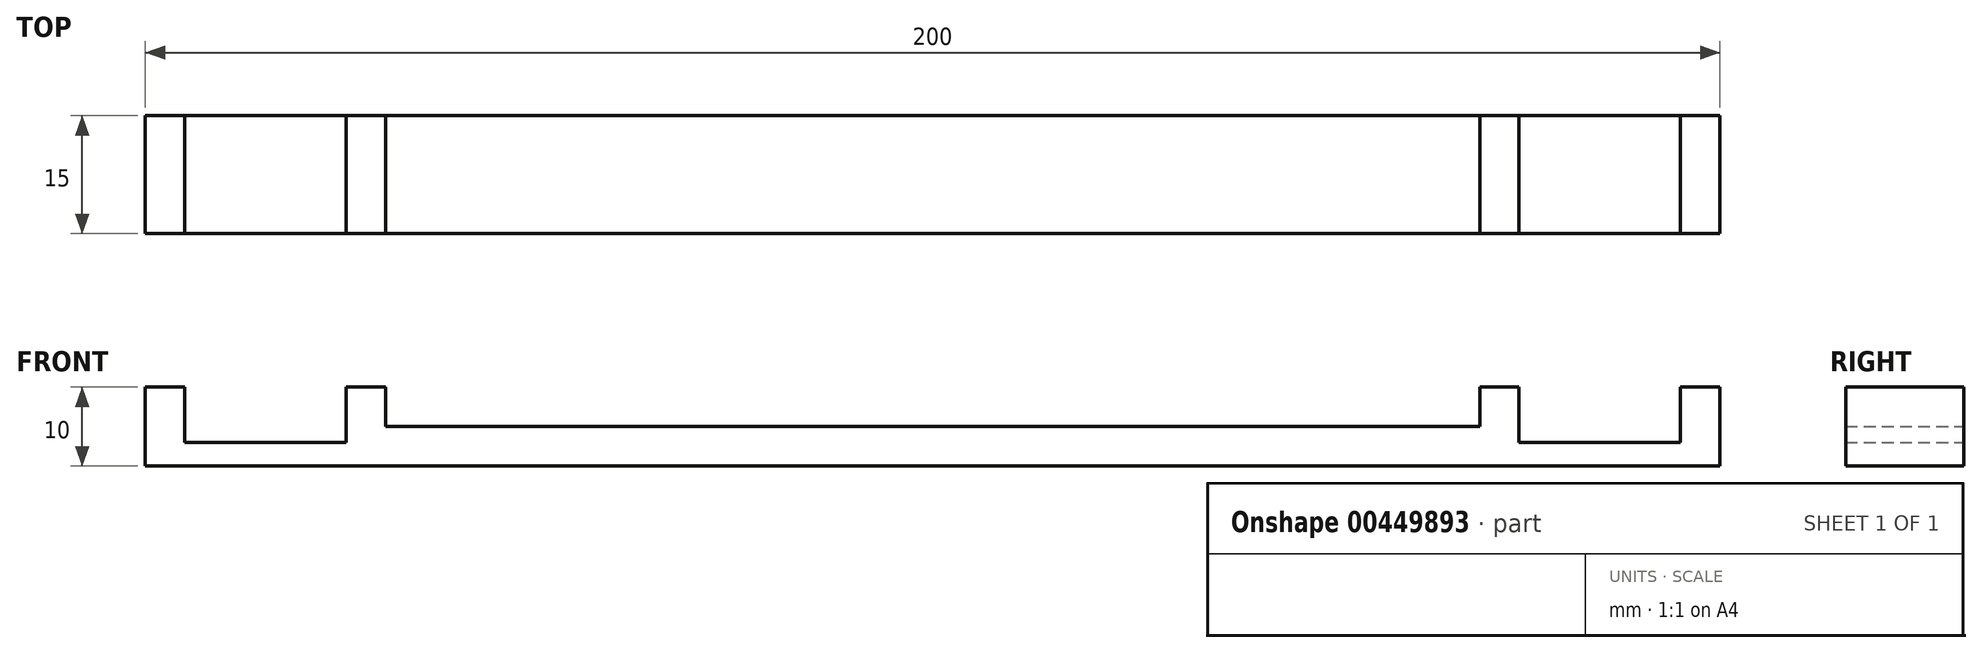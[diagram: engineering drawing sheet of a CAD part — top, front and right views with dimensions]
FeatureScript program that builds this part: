
annotation { "Feature Type Name" : "Feature", "Feature Type Description" : "" }
export const myFeature = defineFeature(function(context is Context, id is Id, definition is map)
    precondition{}
    {
        {
            var Q0;
            Q0=qCreatedBy(makeId("Front.planeOp"),FACE);
            var sketch = newSketch(context, id + "F0", { "sketchPlane" : qUnion([Q0])});
            skLineSegment(sketch, "E0", {"start": v(0, 0) * mm, "end": v(200, 0) * mm});
            skLineSegment(sketch, "E1", {"start": v(0, 0) * mm, "end": v(0, 10) * mm});
            skLineSegment(sketch, "E2", {"start": v(0, 10) * mm, "end": v(5, 10) * mm});
            skLineSegment(sketch, "E3", {"start": v(5, 10) * mm, "end": v(5, 3) * mm});
            skLineSegment(sketch, "E4", {"start": v(5, 3) * mm, "end": v(25.5, 3) * mm});
            skLineSegment(sketch, "E5", {"start": v(25.5, 3) * mm, "end": v(25.5, 10) * mm});
            skLineSegment(sketch, "E6", {"start": v(25.5, 10) * mm, "end": v(30.5, 10) * mm});
            skLineSegment(sketch, "E7", {"start": v(30.5, 10) * mm, "end": v(30.5, 5) * mm});
            skLineSegment(sketch, "E8", {"start": v(30.5, 5) * mm, "end": v(169.5, 5) * mm});
            skLineSegment(sketch, "E9", {"start": v(169.5, 5) * mm, "end": v(169.5, 10) * mm});
            skLineSegment(sketch, "E10", {"start": v(169.5, 10) * mm, "end": v(174.5, 10) * mm});
            skLineSegment(sketch, "E11", {"start": v(174.5, 10) * mm, "end": v(174.5, 3) * mm});
            skLineSegment(sketch, "E12", {"start": v(174.5, 3) * mm, "end": v(195, 3) * mm});
            skLineSegment(sketch, "E13", {"start": v(195, 3) * mm, "end": v(195, 10) * mm});
            skLineSegment(sketch, "E14", {"start": v(195, 10) * mm, "end": v(200, 10) * mm});
            skLineSegment(sketch, "E15", {"start": v(200, 10) * mm, "end": v(200, 0) * mm});
            skSolve(sketch);
        }
        {
            var Q0;
            Q0 = qSketchRegion(id + "F0", true);
            extrude(context, id + "F1", {"entities" : qUnion([Q0]), "depth" : 15 * mm});
        }
    });
